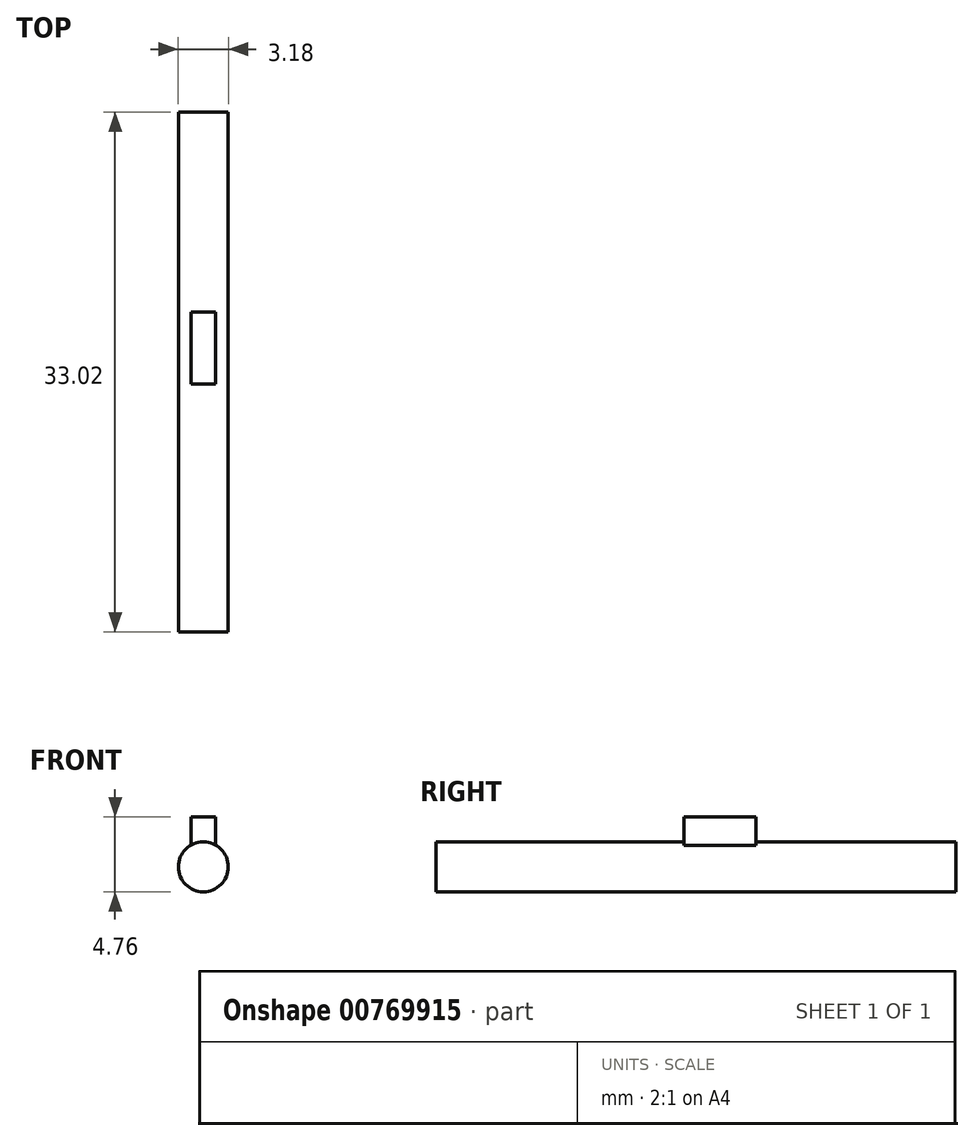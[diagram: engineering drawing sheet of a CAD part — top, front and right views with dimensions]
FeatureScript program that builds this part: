
annotation { "Feature Type Name" : "Feature", "Feature Type Description" : "" }
export const myFeature = defineFeature(function(context is Context, id is Id, definition is map)
    precondition{}
    {
        {
            var Q0;
            Q0=qCreatedBy(makeId("Front.planeOp"),FACE);
            var sketch = newSketch(context, id + "F0", { "sketchPlane" : qUnion([Q0])});
            skCircle(sketch, "E0", {"center": v(0, 0) * mm, "radius": 1.59 * mm});
            skLineSegment(sketch, "E1", {"start": v(-0.8, 1.37) * mm, "end": v(-0.8, 3.17) * mm});
            skLineSegment(sketch, "E2", {"start": v(-0.8, 3.17) * mm, "end": v(0.8, 3.17) * mm});
            skLineSegment(sketch, "E3", {"start": v(0.8, 3.17) * mm, "end": v(0.8, 1.37) * mm});
            skSolve(sketch);
        }
        {
            var Q0;
            {var subQ0=sQuery(id+"F0.wireOp",EDGE,"E1");Q0=makeQuery(id+"F0.imprint","IMPRINT",FACE,{"disambiguationData":[TD([[makeQuery(id+"F0.imprint","IMPRINT",EDGE,{"derivedFrom":subQ0}),-1.0]])]});}
            extrude(context, id + "F1", {"entities" : qUnion([Q0]), "depth" : 4.57 * mm, "offsetDistance" : 25.4 * mm});
        }
        {
            var Q0;
            {var subQ0=sQuery(id+"F0.wireOp",EDGE,"E0");var subQ1=makeQuery(id+"F0.imprint","INTERSECT",VERTEX,{"derivedFrom":[subQ0,sQuery(id+"F0.wireOp",EDGE,"E1")]});Q0=makeQuery(id+"F0.imprint","IMPRINT",FACE,{"disambiguationData":[TD([[makeQuery(id+"F0.imprint","IMPRINT",EDGE,{"disambiguationData":[TD([[subQ1,1.0]])],"derivedFrom":subQ0}),1.0]])]});}
            extrude(context, id + "F2", {"entities" : qUnion([Q0]), "operationType" : NewBodyOperationType.ADD, "depth" : 20.32 * mm, "offsetDistance" : 25.4 * mm});
        }
        {
            var Q0;
            {var subQ0=sQuery(id+"F0.wireOp",EDGE,"E0");Q0=makeQuery(id+"F2.boolean.opBoolean","MERGE",FACE,{"derivedFrom":[makeQuery(id+"F1.opExtrude","CAP_FACE",FACE,{"disambiguationData":[OSD([subQ0,sQuery(id+"F0.wireOp",EDGE,"E1"),sQuery(id+"F0.wireOp",EDGE,"E2"),sQuery(id+"F0.wireOp",EDGE,"E3")])],"isStart":true}),makeQuery(id+"F2.opExtrude","CAP_FACE",FACE,{"disambiguationData":[OSD([subQ0])],"isStart":true})]});}
            var sketch = newSketch(context, id + "F3", { "sketchPlane" : qUnion([Q0])});
            skCircle(sketch, "E4", {"center": v(0, 0) * mm, "radius": 1.59 * mm});
            skSolve(sketch);
        }
        {
            var Q0;
            Q0 = qSketchRegion(id + "F3", true);
            extrude(context, id + "F4", {"entities" : qUnion([Q0]), "operationType" : NewBodyOperationType.ADD, "depth" : 12.7 * mm, "offsetDistance" : 25.4 * mm});
        }
    });
